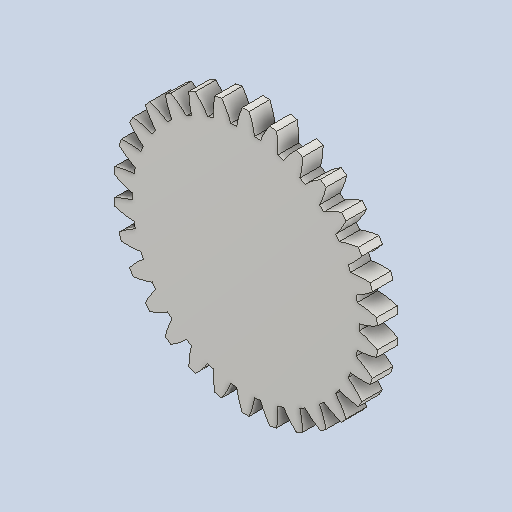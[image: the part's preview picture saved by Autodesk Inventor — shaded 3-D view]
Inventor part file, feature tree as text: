
AUTODESK INVENTOR PART (.ipt)
format: ipt  version: 2024 (Build 280153000, 153)  size: 258,560 bytes
history: native  units: mm (DEFAULTED — no unit token found)
features: plane x3, other x3, extrude x1, sketch x1
ambient origin geometry x8: Origin, YZ Plane, XZ Plane, XY Plane, X Axis, Y Axis, Z Axis, Center Point
bodies: Solid1 (feature_tree)
feature tree (8):
  extrude  "Extrusion1"  Depth=5.0mm TaperAngle=0.0deg
  plane  "Work Plane2"
  plane  "Work Plane8"
  plane  "Work Plane9"
  other  "Spur Gear"
  sketch  "Sketch1"  dims[d0=64.0mm d1=5.0mm d2=0.0mm d3=60.0mm d4=10.0mm d5=0.0mm d16=40.0mm d17=0.0mm d34=1.047198mm d39=0.0mm d41=0.0mm d43=40.0mm d46=40.0mm d47=0.0mm d48=0.0mm]
  other  "Srf1"
  other  "Pitch Diameter"
